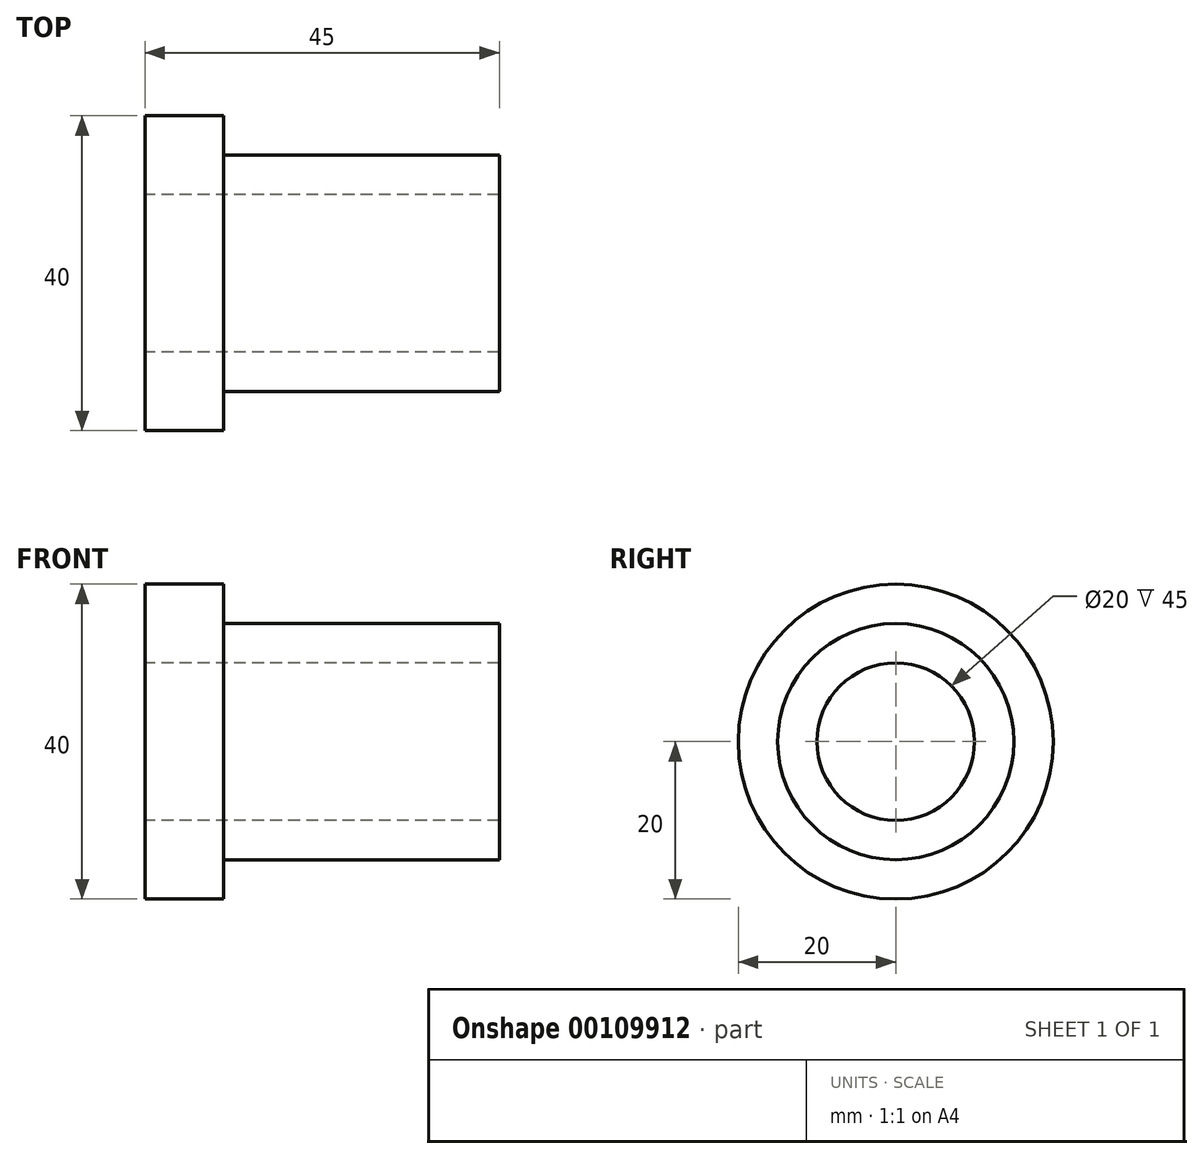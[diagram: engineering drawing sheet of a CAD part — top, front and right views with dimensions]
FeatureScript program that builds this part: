
annotation { "Feature Type Name" : "Feature", "Feature Type Description" : "" }
export const myFeature = defineFeature(function(context is Context, id is Id, definition is map)
    precondition{}
    {
        {
            var Q0;
            Q0=qCreatedBy(makeId("Front.planeOp"),FACE);
            var sketch = newSketch(context, id + "F0", { "sketchPlane" : qUnion([Q0])});
            skLineSegment(sketch, "E0", {"start": v(-1.43, 20) * mm, "end": v(8.57, 20) * mm});
            skLineSegment(sketch, "E1", {"start": v(8.57, 20) * mm, "end": v(8.57, 15) * mm});
            skLineSegment(sketch, "E2", {"start": v(8.57, 15) * mm, "end": v(43.57, 15) * mm});
            skLineSegment(sketch, "E3", {"start": v(43.57, 15) * mm, "end": v(43.57, 10) * mm});
            skLineSegment(sketch, "E4", {"start": v(-1.43, 10) * mm, "end": v(43.57, 10) * mm});
            skLineSegment(sketch, "E5", {"start": v(-1.43, 20) * mm, "end": v(-1.43, 10) * mm});
            skLineSegment(sketch, "E6", {"start": v(0, 0) * mm, "end": v(46.57, 0) * mm, "construction": true});
            skSolve(sketch);
        }
        {
            var Q0;
            Q0=makeQuery(id+"F0.imprint","IMPRINT",FACE,{"disambiguationData":[TD([[makeQuery(id+"F0.imprint","IMPRINT",EDGE,{"derivedFrom":sQuery(id+"F0.wireOp",EDGE,"E0")}),-1.0]])]});
            var Q1;
            Q1=sQuery(id+"F0.wireOp",EDGE,"E6");
            revolve(context, id + "F1", {"entities" : qUnion([Q0]), "axis" : qUnion([Q1]), "revolveType" : RevolveType.FULL});
        }
    });
